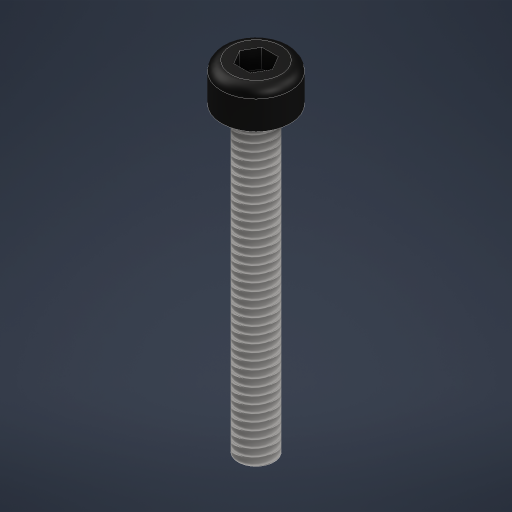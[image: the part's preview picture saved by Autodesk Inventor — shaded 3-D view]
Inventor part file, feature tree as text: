
AUTODESK INVENTOR PART (.ipt)
format: ipt  version: 2024 (Build 280153000, 153)  size: 245,248 bytes
history: native  units: mm
features: extrude x3, sketch x1, fillet x1, thread x1
ambient origin geometry x8: Origin, YZ Plane, XZ Plane, XY Plane, X Axis, Y Axis, Z Axis, Center Point
bodies: Solid1 (feature_tree)
feature tree (6):
  sketch  "Sketch1"  dims[d0=1.9mm d1=3.65mm d2=2.0mm d3=0.0mm d4=16.0mm d5=0.0mm d8=1.5mm d9=1.0mm d10=0.0mm d11=0.5mm d12=16.0mm d13=0.0mm]
  extrude  "Extrusion1"  Depth=16.0mm
  extrude  "Extrusion2"  Depth=2.0mm TaperAngle=0.0deg
  extrude  "Extrusion3"  Depth=16.0mm
  fillet  "Fillet1"  [1 undecoded]
  thread  "Thread2"  [1 undecoded]
note: 2 required parameter values undecoded (feature->parameter linkage not recoverable at this tier; creation-order binding heuristic only, values carry confidence <= 0.55)
